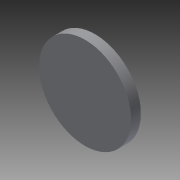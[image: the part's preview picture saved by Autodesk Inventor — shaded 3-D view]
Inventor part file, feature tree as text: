
AUTODESK INVENTOR PART (.ipt)
format: ipt  version: 2015 (Build 190159000, 159)  size: 70,144 bytes
history: native  units: mm
features: extrude x1, sketch x1
ambient origin geometry x8: Origin, YZ Plane, XZ Plane, XY Plane, X Axis, Y Axis, Z Axis, Center Point
bodies: Solid1 (feature_tree)
feature tree (2):
  extrude  "Extrusion1"  Depth=3.0mm TaperAngle=0.0deg
  sketch  "Sketch1"  dims[d0=28.0mm d1=3.0mm d2=0.0mm]
